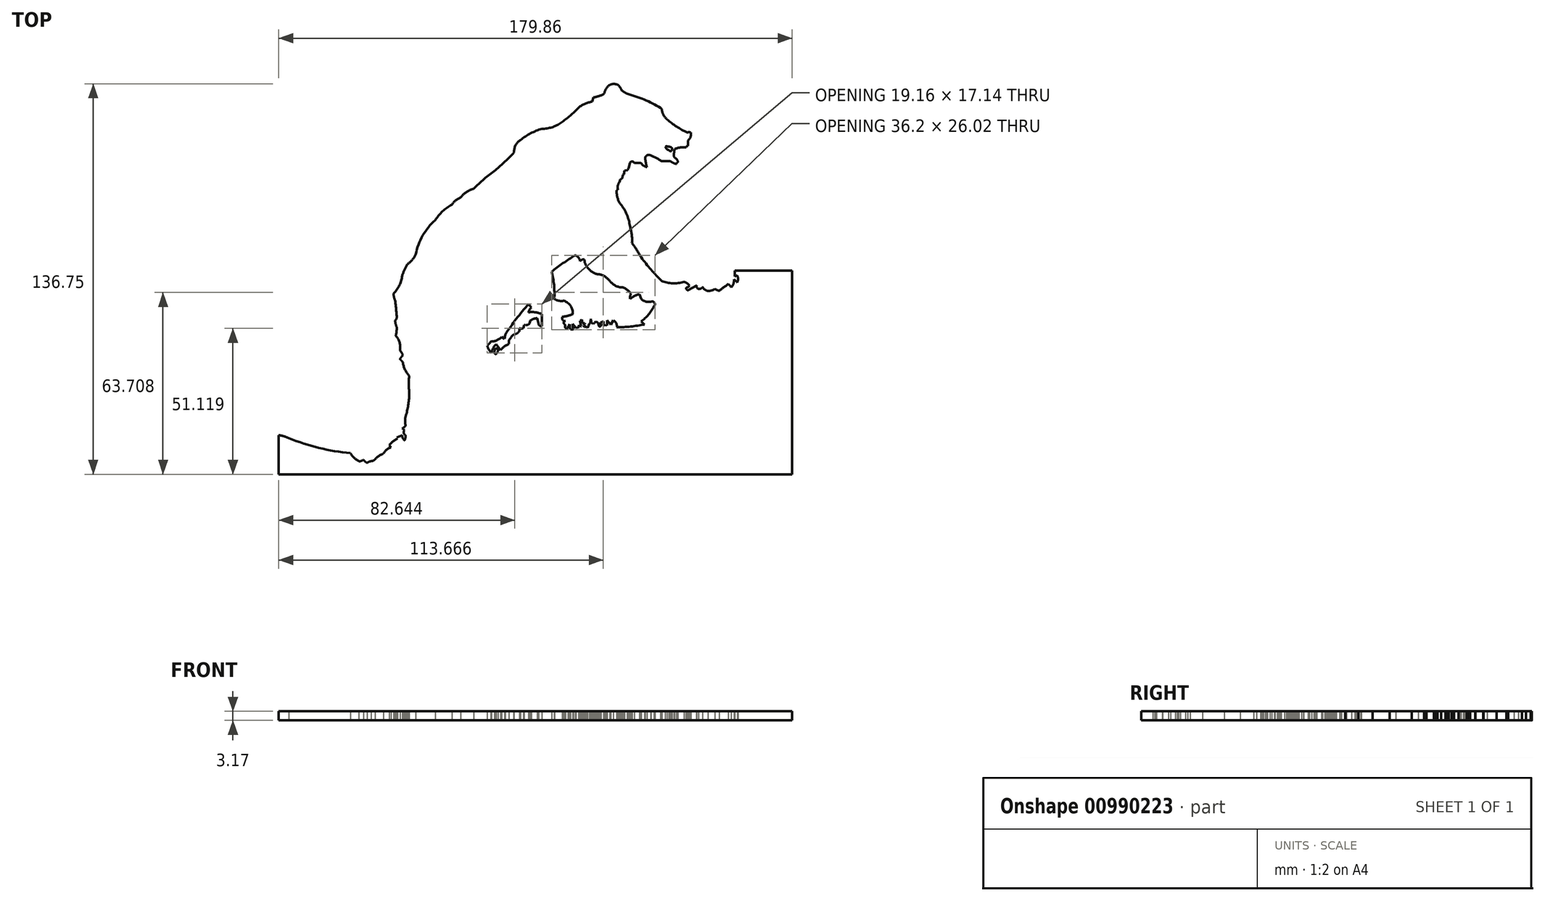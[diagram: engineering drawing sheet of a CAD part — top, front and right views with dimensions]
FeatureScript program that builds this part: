
annotation { "Feature Type Name" : "Feature", "Feature Type Description" : "" }
export const myFeature = defineFeature(function(context is Context, id is Id, definition is map)
    precondition{}
    {
        {
            var Q0;
            Q0=qCreatedBy(makeId("Top.planeOp"),FACE);
            var sketch = newSketch(context, id + "F0", { "sketchPlane" : qUnion([Q0])});
            skArc(sketch, "E0", {"start": v(84.74, 117.13) * mm, "mid": v(82.97, 115.24) * mm, "end": v(82.44, 112.7) * mm});
            skArc(sketch, "E1", {"start": v(75.9, 106.56) * mm, "mid": v(79.27, 109.53) * mm, "end": v(82.44, 112.7) * mm});
            skArc(sketch, "E2", {"start": v(75.9, 106.56) * mm, "mid": v(71.95, 103.44) * mm, "end": v(68.26, 100.02) * mm});
            skArc(sketch, "E3", {"start": v(68.26, 100.02) * mm, "mid": v(67.47, 99.77) * mm, "end": v(66.7, 99.44) * mm});
            skArc(sketch, "E4", {"start": v(66.7, 99.44) * mm, "mid": v(65.08, 98.39) * mm, "end": v(63.77, 96.95) * mm});
            skArc(sketch, "E5", {"start": v(63.77, 96.95) * mm, "mid": v(62.01, 95.94) * mm, "end": v(60.66, 94.42) * mm});
            skArc(sketch, "E6", {"start": v(60.66, 94.42) * mm, "mid": v(57.42, 92.12) * mm, "end": v(54.88, 89.06) * mm});
            skArc(sketch, "E7", {"start": v(54.88, 89.06) * mm, "mid": v(50.44, 83.63) * mm, "end": v(48, 77.05) * mm});
            skArc(sketch, "E8", {"start": v(45.04, 73.58) * mm, "mid": v(46.77, 75.1) * mm, "end": v(48, 77.05) * mm});
            skArc(sketch, "E9", {"start": v(45.04, 73.58) * mm, "mid": v(44.05, 71.63) * mm, "end": v(43.23, 69.6) * mm});
            skArc(sketch, "E10", {"start": v(40.26, 63.38) * mm, "mid": v(42.3, 66.22) * mm, "end": v(43.23, 69.6) * mm});
            skArc(sketch, "E11", {"start": v(40.26, 63.38) * mm, "mid": v(40.38, 62.12) * mm, "end": v(40.77, 60.92) * mm});
            skArc(sketch, "E12", {"start": v(41.35, 55.06) * mm, "mid": v(41.1, 58) * mm, "end": v(40.77, 60.92) * mm});
            skArc(sketch, "E13", {"start": v(40.77, 53.87) * mm, "mid": v(41.2, 54.4) * mm, "end": v(41.35, 55.06) * mm});
            skArc(sketch, "E14", {"start": v(40.77, 53.87) * mm, "mid": v(40.96, 52.69) * mm, "end": v(41.35, 51.55) * mm});
            skArc(sketch, "E15", {"start": v(41.02, 48.52) * mm, "mid": v(41.28, 50.03) * mm, "end": v(41.35, 51.55) * mm});
            skArc(sketch, "E16", {"start": v(42.47, 43.34) * mm, "mid": v(42.37, 46.1) * mm, "end": v(41.02, 48.52) * mm});
            skArc(sketch, "E17", {"start": v(43.48, 41.72) * mm, "mid": v(43.1, 42.6) * mm, "end": v(42.47, 43.34) * mm});
            skArc(sketch, "E18", {"start": v(43.48, 41.72) * mm, "mid": v(42.92, 41.07) * mm, "end": v(42.47, 40.34) * mm});
            skArc(sketch, "E19", {"start": v(43.48, 39.26) * mm, "mid": v(42.98, 39.8) * mm, "end": v(42.47, 40.34) * mm});
            skArc(sketch, "E20", {"start": v(43.48, 39.26) * mm, "mid": v(44.22, 36.72) * mm, "end": v(45.72, 34.55) * mm});
            skArc(sketch, "E21", {"start": v(45.72, 34.55) * mm, "mid": v(45.54, 31.76) * mm, "end": v(45.72, 28.96) * mm});
            skArc(sketch, "E22", {"start": v(44.76, 21.36) * mm, "mid": v(45.5, 25.13) * mm, "end": v(45.72, 28.96) * mm});
            skArc(sketch, "E23", {"start": v(44.76, 21.36) * mm, "mid": v(44.28, 19.27) * mm, "end": v(44.47, 17.14) * mm});
            skArc(sketch, "E24", {"start": v(43.23, 16.13) * mm, "mid": v(43.96, 16.5) * mm, "end": v(44.47, 17.14) * mm});
            skArc(sketch, "E25", {"start": v(44.04, 15.47) * mm, "mid": v(43.65, 15.82) * mm, "end": v(43.23, 16.13) * mm});
            skArc(sketch, "E26", {"start": v(44.04, 15.47) * mm, "mid": v(43.8, 14.48) * mm, "end": v(44.47, 13.7) * mm});
            skArc(sketch, "E27", {"start": v(44.04, 11.87) * mm, "mid": v(44.4, 12.75) * mm, "end": v(44.47, 13.7) * mm});
            skArc(sketch, "E28", {"start": v(43.23, 13.7) * mm, "mid": v(43.48, 12.71) * mm, "end": v(44.04, 11.87) * mm});
            skLineSegment(sketch, "E29", {"start": v(43.23, 13.7) * mm, "end": v(41.39, 12.99) * mm});
            skLineSegment(sketch, "E30", {"start": v(41.39, 12.99) * mm, "end": v(41.57, 12.5) * mm});
            skArc(sketch, "E31", {"start": v(41.57, 12.5) * mm, "mid": v(40.04, 11.56) * mm, "end": v(38.76, 10.28) * mm});
            skArc(sketch, "E32", {"start": v(39.36, 9.44) * mm, "mid": v(37.78, 8.63) * mm, "end": v(36.66, 7.25) * mm});
            skArc(sketch, "E33", {"start": v(36.66, 7.25) * mm, "mid": v(35.1, 6.45) * mm, "end": v(33.8, 5.3) * mm});
            skArc(sketch, "E34", {"start": v(32.36, 4.63) * mm, "mid": v(33.15, 4.8) * mm, "end": v(33.8, 5.3) * mm});
            skArc(sketch, "E35", {"start": v(32.36, 4.63) * mm, "mid": v(31.6, 4.4) * mm, "end": v(30.92, 4.02) * mm});
            skArc(sketch, "E36", {"start": v(29.64, 5.1) * mm, "mid": v(30.27, 4.55) * mm, "end": v(30.92, 4.02) * mm});
            skArc(sketch, "E37", {"start": v(28.03, 4.63) * mm, "mid": v(28.9, 4.68) * mm, "end": v(29.64, 5.1) * mm});
            skLineSegment(sketch, "E38", {"start": v(39.36, 9.44) * mm, "end": v(38.76, 10.28) * mm});
            skArc(sketch, "E39", {"start": v(25.08, 7.49) * mm, "mid": v(26.36, 5.86) * mm, "end": v(28.03, 4.63) * mm});
            skArc(sketch, "E40", {"start": v(3.55, 12.71) * mm, "mid": v(14.1, 9.26) * mm, "end": v(25.08, 7.49) * mm});
            skArc(sketch, "E41", {"start": v(3.55, 12.71) * mm, "mid": v(1.81, 13.35) * mm, "end": v(0, 13.7) * mm});
            skArc(sketch, "E42", {"start": v(92.2, 121.04) * mm, "mid": v(88.28, 119.45) * mm, "end": v(84.74, 117.13) * mm});
            skArc(sketch, "E43", {"start": v(92.2, 121.04) * mm, "mid": v(95.7, 121.57) * mm, "end": v(98.86, 123.14) * mm});
            skArc(sketch, "E44", {"start": v(98.86, 123.14) * mm, "mid": v(102.08, 125.64) * mm, "end": v(105.06, 128.42) * mm});
            skArc(sketch, "E45", {"start": v(109.8, 130.52) * mm, "mid": v(107.28, 129.82) * mm, "end": v(105.06, 128.42) * mm});
            skArc(sketch, "E46", {"start": v(110.16, 132.02) * mm, "mid": v(112.17, 132.46) * mm, "end": v(114.04, 133.3) * mm});
            skArc(sketch, "E47", {"start": v(115.9, 136.35) * mm, "mid": v(114.66, 135.01) * mm, "end": v(114.04, 133.3) * mm});
            skArc(sketch, "E48", {"start": v(118.82, 136.35) * mm, "mid": v(117.36, 136.75) * mm, "end": v(115.9, 136.35) * mm});
            skArc(sketch, "E49", {"start": v(120.05, 134.62) * mm, "mid": v(119.55, 135.57) * mm, "end": v(118.82, 136.35) * mm});
            skArc(sketch, "E50", {"start": v(120.05, 134.62) * mm, "mid": v(121, 133.9) * mm, "end": v(122.06, 133.3) * mm});
            skArc(sketch, "E51", {"start": v(133.72, 128.42) * mm, "mid": v(128.05, 131.24) * mm, "end": v(122.06, 133.3) * mm});
            skArc(sketch, "E52", {"start": v(134.23, 127.88) * mm, "mid": v(134.74, 125.93) * mm, "end": v(136, 124.37) * mm});
            skArc(sketch, "E53", {"start": v(136, 124.37) * mm, "mid": v(139.39, 121.78) * mm, "end": v(143.11, 119.72) * mm});
            skArc(sketch, "E54", {"start": v(144.32, 119.72) * mm, "mid": v(143.72, 119.84) * mm, "end": v(143.11, 119.72) * mm});
            skArc(sketch, "E55", {"start": v(143.37, 116.96) * mm, "mid": v(144.26, 118.2) * mm, "end": v(144.32, 119.72) * mm});
            skLineSegment(sketch, "E56", {"start": v(134.23, 127.88) * mm, "end": v(133.72, 128.42) * mm});
            skLineSegment(sketch, "E57", {"start": v(143.37, 116.96) * mm, "end": v(143.37, 115.1) * mm});
            skArc(sketch, "E58", {"start": v(143.37, 115.1) * mm, "mid": v(142.93, 114.88) * mm, "end": v(142.64, 114.48) * mm});
            skArc(sketch, "E59", {"start": v(142.64, 114.48) * mm, "mid": v(140.65, 114.49) * mm, "end": v(138.72, 113.95) * mm});
            skArc(sketch, "E60", {"start": v(138.72, 113.95) * mm, "mid": v(138.47, 112.51) * mm, "end": v(138.5, 111.05) * mm});
            skArc(sketch, "E61", {"start": v(137.65, 114.48) * mm, "mid": v(136.55, 114.8) * mm, "end": v(135.4, 114.84) * mm});
            skArc(sketch, "E62", {"start": v(135.4, 114.84) * mm, "mid": v(135.86, 113.98) * mm, "end": v(136.7, 113.52) * mm});
            skArc(sketch, "E63", {"start": v(136.7, 113.52) * mm, "mid": v(137.03, 113.25) * mm, "end": v(137.45, 113.2) * mm});
            skArc(sketch, "E64", {"start": v(137.45, 113.2) * mm, "mid": v(137.73, 113.81) * mm, "end": v(137.65, 114.48) * mm});
            skArc(sketch, "E65", {"start": v(139.86, 109.47) * mm, "mid": v(139.34, 110.4) * mm, "end": v(138.5, 111.05) * mm});
            skArc(sketch, "E66", {"start": v(139.86, 109.47) * mm, "mid": v(139.5, 109.11) * mm, "end": v(139.28, 108.66) * mm});
            skArc(sketch, "E67", {"start": v(137.1, 109.7) * mm, "mid": v(138.15, 109.1) * mm, "end": v(139.28, 108.66) * mm});
            skArc(sketch, "E68", {"start": v(134.12, 109.7) * mm, "mid": v(132.23, 110.8) * mm, "end": v(130.24, 111.74) * mm});
            skArc(sketch, "E69", {"start": v(130.24, 111.74) * mm, "mid": v(128.93, 111.71) * mm, "end": v(128.37, 110.53) * mm});
            skLineSegment(sketch, "E70", {"start": v(137.1, 109.7) * mm, "end": v(134.12, 109.7) * mm});
            skArc(sketch, "E71", {"start": v(128.37, 110.53) * mm, "mid": v(128.6, 109.05) * mm, "end": v(128.98, 107.6) * mm});
            skArc(sketch, "E72", {"start": v(126.9, 109.12) * mm, "mid": v(127.77, 108.13) * mm, "end": v(128.98, 107.6) * mm});
            skArc(sketch, "E73", {"start": v(124.53, 109.12) * mm, "mid": v(123.78, 109.6) * mm, "end": v(123.03, 109.12) * mm});
            skLineSegment(sketch, "E74", {"start": v(126.9, 109.12) * mm, "end": v(124.53, 109.12) * mm});
            skLineSegment(sketch, "E75", {"start": v(123.03, 109.12) * mm, "end": v(122.57, 107.17) * mm});
            skLineSegment(sketch, "E76", {"start": v(122.57, 107.17) * mm, "end": v(122.3, 106.86) * mm});
            skLineSegment(sketch, "E77", {"start": v(122.3, 106.86) * mm, "end": v(122.3, 106.6) * mm});
            skLineSegment(sketch, "E78", {"start": v(122.3, 106.6) * mm, "end": v(121.12, 106.45) * mm});
            skLineSegment(sketch, "E79", {"start": v(121.12, 106.45) * mm, "end": v(120.9, 105.02) * mm});
            skLineSegment(sketch, "E80", {"start": v(120.9, 105.02) * mm, "end": v(120.54, 104.91) * mm});
            skLineSegment(sketch, "E81", {"start": v(120.54, 104.91) * mm, "end": v(120.42, 103.68) * mm});
            skLineSegment(sketch, "E82", {"start": v(120.42, 103.68) * mm, "end": v(120, 103.51) * mm});
            skLineSegment(sketch, "E83", {"start": v(120, 103.51) * mm, "end": v(119.57, 103.22) * mm});
            skLineSegment(sketch, "E84", {"start": v(119.57, 103.22) * mm, "end": v(119.36, 102.38) * mm});
            skArc(sketch, "E85", {"start": v(119.36, 102.38) * mm, "mid": v(118.79, 101.13) * mm, "end": v(118.84, 99.76) * mm});
            skArc(sketch, "E86", {"start": v(118.84, 99.76) * mm, "mid": v(118.45, 99.5) * mm, "end": v(118.38, 99.04) * mm});
            skArc(sketch, "E87", {"start": v(118.38, 99.04) * mm, "mid": v(118.71, 96.72) * mm, "end": v(119.73, 94.62) * mm});
            skArc(sketch, "E88", {"start": v(123, 86.95) * mm, "mid": v(121.92, 91.02) * mm, "end": v(119.73, 94.62) * mm});
            skArc(sketch, "E89", {"start": v(123.74, 81) * mm, "mid": v(123.66, 84.01) * mm, "end": v(123, 86.95) * mm});
            skArc(sketch, "E90", {"start": v(126.93, 76.01) * mm, "mid": v(125.44, 78.58) * mm, "end": v(123.74, 81) * mm});
            skArc(sketch, "E91", {"start": v(126.93, 76.01) * mm, "mid": v(130.4, 71.72) * mm, "end": v(134.16, 67.69) * mm});
            skArc(sketch, "E92", {"start": v(134.16, 67.69) * mm, "mid": v(138.01, 66.92) * mm, "end": v(141.91, 67.43) * mm});
            skArc(sketch, "E93", {"start": v(143.83, 66.14) * mm, "mid": v(142.98, 66.95) * mm, "end": v(141.91, 67.43) * mm});
            skArc(sketch, "E94", {"start": v(142.8, 65.45) * mm, "mid": v(143.43, 65.62) * mm, "end": v(143.83, 66.14) * mm});
            skArc(sketch, "E95", {"start": v(142.8, 65.45) * mm, "mid": v(142.83, 64.8) * mm, "end": v(143.38, 64.47) * mm});
            skArc(sketch, "E96", {"start": v(103.02, 56.1) * mm, "mid": v(102.27, 58.99) * mm, "end": v(99.9, 60.8) * mm});
            skArc(sketch, "E97", {"start": v(96.5, 61.46) * mm, "mid": v(96.44, 66.27) * mm, "end": v(95.57, 71) * mm});
            skArc(sketch, "E98", {"start": v(103.81, 76.72) * mm, "mid": v(99.61, 73.97) * mm, "end": v(95.57, 71) * mm});
            skArc(sketch, "E99", {"start": v(99.26, 55.16) * mm, "mid": v(101.17, 55.51) * mm, "end": v(103.02, 56.1) * mm});
            skArc(sketch, "E100", {"start": v(131.48, 58.89) * mm, "mid": v(131.6, 60.14) * mm, "end": v(130.4, 60.48) * mm});
            skArc(sketch, "E101", {"start": v(126.93, 61.46) * mm, "mid": v(128.53, 60.5) * mm, "end": v(130.4, 60.48) * mm});
            skArc(sketch, "E102", {"start": v(126.38, 63.08) * mm, "mid": v(124.59, 62.48) * mm, "end": v(123, 61.46) * mm});
            skArc(sketch, "E103", {"start": v(123.41, 63.3) * mm, "mid": v(123.08, 62.4) * mm, "end": v(123, 61.46) * mm});
            skArc(sketch, "E104", {"start": v(123.41, 63.3) * mm, "mid": v(122.22, 64.53) * mm, "end": v(120.77, 65.45) * mm});
            skArc(sketch, "E105", {"start": v(116.18, 67.43) * mm, "mid": v(118.26, 65.94) * mm, "end": v(120.77, 65.45) * mm});
            skArc(sketch, "E106", {"start": v(116.18, 67.43) * mm, "mid": v(114.5, 69.1) * mm, "end": v(112.34, 70.06) * mm});
            skArc(sketch, "E107", {"start": v(108.76, 71.8) * mm, "mid": v(110.36, 70.54) * mm, "end": v(112.34, 70.06) * mm});
            skArc(sketch, "E108", {"start": v(107.06, 75.3) * mm, "mid": v(107.56, 73.38) * mm, "end": v(108.76, 71.8) * mm});
            skArc(sketch, "E109", {"start": v(107.06, 75.3) * mm, "mid": v(106.23, 75.18) * mm, "end": v(105.54, 74.7) * mm});
            skArc(sketch, "E110", {"start": v(105.54, 74.7) * mm, "mid": v(105, 75.98) * mm, "end": v(103.81, 76.72) * mm});
            skArc(sketch, "E111", {"start": v(126.93, 53.55) * mm, "mid": v(129.53, 55.93) * mm, "end": v(131.48, 58.89) * mm});
            skArc(sketch, "E112", {"start": v(118.38, 51.5) * mm, "mid": v(123.26, 51.78) * mm, "end": v(128.1, 52.5) * mm});
            skArc(sketch, "E113", {"start": v(118.38, 51.5) * mm, "mid": v(118.22, 52.9) * mm, "end": v(117.21, 53.9) * mm});
            skLineSegment(sketch, "E114", {"start": v(128.1, 52.5) * mm, "end": v(126.93, 53.55) * mm});
            skLineSegment(sketch, "E115", {"start": v(117.21, 53.9) * mm, "end": v(116.25, 52.5) * mm});
            skLineSegment(sketch, "E116", {"start": v(116.25, 52.5) * mm, "end": v(115.07, 53.9) * mm});
            skLineSegment(sketch, "E117", {"start": v(115.07, 53.9) * mm, "end": v(115.07, 52.13) * mm});
            skLineSegment(sketch, "E118", {"start": v(115.07, 52.13) * mm, "end": v(114.56, 52.32) * mm});
            skLineSegment(sketch, "E119", {"start": v(114.56, 52.32) * mm, "end": v(114.05, 52.13) * mm});
            skLineSegment(sketch, "E120", {"start": v(114.05, 52.13) * mm, "end": v(113.71, 52.32) * mm});
            skLineSegment(sketch, "E121", {"start": v(113.71, 52.32) * mm, "end": v(113.71, 53.55) * mm});
            skLineSegment(sketch, "E122", {"start": v(113.71, 53.55) * mm, "end": v(112.77, 53.25) * mm});
            skLineSegment(sketch, "E123", {"start": v(112.77, 53.25) * mm, "end": v(112.9, 52.13) * mm});
            skLineSegment(sketch, "E124", {"start": v(112.08, 52.1) * mm, "end": v(111.83, 53.01) * mm});
            skLineSegment(sketch, "E125", {"start": v(111.83, 53.01) * mm, "end": v(111.43, 53.37) * mm});
            skLineSegment(sketch, "E126", {"start": v(111.43, 53.37) * mm, "end": v(111.1, 53.46) * mm});
            skLineSegment(sketch, "E127", {"start": v(111.1, 53.46) * mm, "end": v(110.64, 53.21) * mm});
            skLineSegment(sketch, "E128", {"start": v(110.64, 53.21) * mm, "end": v(110.56, 52.8) * mm});
            skLineSegment(sketch, "E129", {"start": v(110.56, 52.8) * mm, "end": v(109.6, 52.96) * mm});
            skLineSegment(sketch, "E130", {"start": v(109.6, 52.96) * mm, "end": v(109.33, 54.42) * mm});
            skLineSegment(sketch, "E131", {"start": v(109.33, 54.42) * mm, "end": v(109.03, 52.78) * mm});
            skLineSegment(sketch, "E132", {"start": v(109.03, 52.78) * mm, "end": v(108.76, 52.83) * mm});
            skLineSegment(sketch, "E133", {"start": v(108.76, 52.83) * mm, "end": v(108.25, 51.24) * mm});
            skLineSegment(sketch, "E134", {"start": v(108.25, 51.24) * mm, "end": v(107.8, 51.78) * mm});
            skLineSegment(sketch, "E135", {"start": v(107.8, 51.78) * mm, "end": v(107.1, 51.53) * mm});
            skLineSegment(sketch, "E136", {"start": v(107.1, 51.53) * mm, "end": v(106.73, 52.2) * mm});
            skLineSegment(sketch, "E137", {"start": v(106.73, 52.2) * mm, "end": v(107.29, 52.54) * mm});
            skLineSegment(sketch, "E138", {"start": v(107.29, 52.54) * mm, "end": v(107.13, 52.92) * mm});
            skLineSegment(sketch, "E139", {"start": v(107.13, 52.92) * mm, "end": v(106.44, 52.92) * mm});
            skLineSegment(sketch, "E140", {"start": v(106.44, 52.92) * mm, "end": v(106.2, 54.19) * mm});
            skLineSegment(sketch, "E141", {"start": v(106.2, 54.19) * mm, "end": v(105.9, 53.84) * mm});
            skLineSegment(sketch, "E142", {"start": v(105.9, 53.84) * mm, "end": v(105.57, 53.84) * mm});
            skLineSegment(sketch, "E143", {"start": v(105.57, 53.84) * mm, "end": v(105.95, 51.93) * mm});
            skLineSegment(sketch, "E144", {"start": v(105.95, 51.93) * mm, "end": v(105.68, 51.67) * mm});
            skLineSegment(sketch, "E145", {"start": v(105.68, 51.67) * mm, "end": v(105.08, 52.32) * mm});
            skLineSegment(sketch, "E146", {"start": v(105.08, 52.32) * mm, "end": v(105.08, 51.51) * mm});
            skLineSegment(sketch, "E147", {"start": v(105.08, 51.51) * mm, "end": v(104.1, 51.3) * mm});
            skLineSegment(sketch, "E148", {"start": v(104.1, 51.3) * mm, "end": v(102.95, 52.69) * mm});
            skLineSegment(sketch, "E149", {"start": v(102.95, 52.69) * mm, "end": v(102.95, 51.53) * mm});
            skLineSegment(sketch, "E150", {"start": v(102.95, 51.53) * mm, "end": v(103.24, 50.91) * mm});
            skLineSegment(sketch, "E151", {"start": v(103.24, 50.91) * mm, "end": v(102.93, 50.7) * mm});
            skLineSegment(sketch, "E152", {"start": v(102.93, 50.7) * mm, "end": v(102.24, 50.8) * mm});
            skLineSegment(sketch, "E153", {"start": v(102.24, 50.8) * mm, "end": v(101.95, 51.3) * mm});
            skLineSegment(sketch, "E154", {"start": v(101.95, 51.3) * mm, "end": v(101.94, 52.54) * mm});
            skLineSegment(sketch, "E155", {"start": v(101.94, 52.54) * mm, "end": v(101.63, 51.9) * mm});
            skLineSegment(sketch, "E156", {"start": v(101.63, 51.9) * mm, "end": v(101.3, 51.87) * mm});
            skLineSegment(sketch, "E157", {"start": v(101.3, 51.87) * mm, "end": v(101.32, 51.5) * mm});
            skLineSegment(sketch, "E158", {"start": v(100.36, 51.53) * mm, "end": v(100.36, 52.38) * mm});
            skArc(sketch, "E159", {"start": v(99.26, 55.16) * mm, "mid": v(99.28, 54.53) * mm, "end": v(99.51, 53.93) * mm});
            skArc(sketch, "E160", {"start": v(99.51, 53.93) * mm, "mid": v(99.94, 53.74) * mm, "end": v(100.42, 53.74) * mm});
            skArc(sketch, "E161", {"start": v(100.42, 53.74) * mm, "mid": v(100.02, 53.46) * mm, "end": v(99.8, 53.03) * mm});
            skArc(sketch, "E162", {"start": v(99.8, 53.03) * mm, "mid": v(100.04, 52.67) * mm, "end": v(100.36, 52.38) * mm});
            skArc(sketch, "E163", {"start": v(100.36, 51.53) * mm, "mid": v(100.83, 51.05) * mm, "end": v(101.32, 51.5) * mm});
            skArc(sketch, "E164", {"start": v(112.08, 52.1) * mm, "mid": v(112.5, 51.8) * mm, "end": v(112.9, 52.13) * mm});
            skArc(sketch, "E165", {"start": v(96.5, 61.46) * mm, "mid": v(98.14, 60.8) * mm, "end": v(99.9, 60.8) * mm});
            skLineSegment(sketch, "E166", {"start": v(126.93, 61.46) * mm, "end": v(126.38, 63.08) * mm});
            skLineSegment(sketch, "E167", {"start": v(92.22, 51.95) * mm, "end": v(92.22, 56.07) * mm});
            skArc(sketch, "E168", {"start": v(92.22, 56.07) * mm, "mid": v(89.92, 56.77) * mm, "end": v(87.5, 56.77) * mm});
            skArc(sketch, "E169", {"start": v(88.47, 58.41) * mm, "mid": v(87.86, 57.67) * mm, "end": v(87.5, 56.77) * mm});
            skArc(sketch, "E170", {"start": v(87.5, 59.69) * mm, "mid": v(83.22, 54.45) * mm, "end": v(79.3, 48.93) * mm});
            skArc(sketch, "E171", {"start": v(74.34, 46.52) * mm, "mid": v(76.38, 46.95) * mm, "end": v(78.12, 48.11) * mm});
            skArc(sketch, "E172", {"start": v(90.56, 54.67) * mm, "mid": v(89.29, 54.46) * mm, "end": v(88.15, 53.85) * mm});
            skArc(sketch, "E173", {"start": v(85.96, 52.3) * mm, "mid": v(87.02, 52.32) * mm, "end": v(87.92, 52.9) * mm});
            skArc(sketch, "E174", {"start": v(84.32, 51.21) * mm, "mid": v(85, 51.03) * mm, "end": v(85.69, 51.21) * mm});
            skArc(sketch, "E175", {"start": v(82.27, 48.93) * mm, "mid": v(83.38, 49.35) * mm, "end": v(84.32, 50.07) * mm});
            skArc(sketch, "E176", {"start": v(82.27, 48.93) * mm, "mid": v(81.32, 47.92) * mm, "end": v(80.58, 46.74) * mm});
            skArc(sketch, "E177", {"start": v(80.63, 45.65) * mm, "mid": v(79.02, 44.76) * mm, "end": v(77.67, 43.5) * mm});
            skArc(sketch, "E178", {"start": v(77.67, 43.5) * mm, "mid": v(76.93, 44.57) * mm, "end": v(76.16, 45.6) * mm});
            skArc(sketch, "E179", {"start": v(76.16, 45.6) * mm, "mid": v(75.14, 44.19) * mm, "end": v(74.52, 42.55) * mm});
            skArc(sketch, "E180", {"start": v(73.06, 45.01) * mm, "mid": v(73.62, 43.68) * mm, "end": v(74.52, 42.55) * mm});
            skArc(sketch, "E181", {"start": v(73.06, 45.01) * mm, "mid": v(73.71, 45.75) * mm, "end": v(74.34, 46.52) * mm});
            skArc(sketch, "E182", {"start": v(91.02, 52.67) * mm, "mid": v(91.46, 52.04) * mm, "end": v(92.22, 51.95) * mm});
            skLineSegment(sketch, "E183", {"start": v(91.02, 52.67) * mm, "end": v(90.56, 54.67) * mm});
            skLineSegment(sketch, "E184", {"start": v(88.47, 58.41) * mm, "end": v(87.5, 59.69) * mm});
            skLineSegment(sketch, "E185", {"start": v(79.3, 48.93) * mm, "end": v(79.15, 47.53) * mm});
            skLineSegment(sketch, "E186", {"start": v(79.15, 47.53) * mm, "end": v(78.12, 48.11) * mm});
            skLineSegment(sketch, "E187", {"start": v(80.63, 45.65) * mm, "end": v(80.58, 46.74) * mm});
            skLineSegment(sketch, "E188", {"start": v(84.32, 50.07) * mm, "end": v(84.32, 51.21) * mm});
            skLineSegment(sketch, "E189", {"start": v(85.69, 51.21) * mm, "end": v(85.96, 52.3) * mm});
            skLineSegment(sketch, "E190", {"start": v(88.15, 53.85) * mm, "end": v(87.92, 52.9) * mm});
            skArc(sketch, "E191", {"start": v(76.87, 43.48) * mm, "mid": v(76.33, 44.08) * mm, "end": v(75.62, 43.7) * mm});
            skArc(sketch, "E192", {"start": v(76.22, 42.25) * mm, "mid": v(76.62, 42.82) * mm, "end": v(76.87, 43.48) * mm});
            skArc(sketch, "E193", {"start": v(75.53, 42.7) * mm, "mid": v(75.73, 42.25) * mm, "end": v(76.22, 42.25) * mm});
            skLineSegment(sketch, "E194", {"start": v(75.53, 42.7) * mm, "end": v(75.62, 43.7) * mm});
            skLineSegment(sketch, "E195", {"start": v(143.38, 64.47) * mm, "end": v(146.37, 66.14) * mm});
            skArc(sketch, "E196", {"start": v(146.37, 66.14) * mm, "mid": v(146.44, 65.41) * mm, "end": v(147, 64.96) * mm});
            skArc(sketch, "E197", {"start": v(147, 64.96) * mm, "mid": v(147.84, 65.06) * mm, "end": v(148.44, 65.65) * mm});
            skArc(sketch, "E198", {"start": v(148.44, 65.65) * mm, "mid": v(149.21, 64.73) * mm, "end": v(150.3, 64.24) * mm});
            skArc(sketch, "E199", {"start": v(152.78, 64.96) * mm, "mid": v(153.51, 64.56) * mm, "end": v(154.3, 64.27) * mm});
            skArc(sketch, "E200", {"start": v(157.49, 66.6) * mm, "mid": v(155.83, 65.51) * mm, "end": v(154.3, 64.27) * mm});
            skArc(sketch, "E201", {"start": v(158.5, 65.48) * mm, "mid": v(158.04, 66.08) * mm, "end": v(157.49, 66.6) * mm});
            skArc(sketch, "E202", {"start": v(158.5, 65.48) * mm, "mid": v(159.26, 66.77) * mm, "end": v(159.52, 68.26) * mm});
            skArc(sketch, "E203", {"start": v(160.61, 67.23) * mm, "mid": v(160.1, 67.77) * mm, "end": v(159.52, 68.26) * mm});
            skArc(sketch, "E204", {"start": v(150.3, 64.24) * mm, "mid": v(151.6, 64.4) * mm, "end": v(152.78, 64.96) * mm});
            skArc(sketch, "E205", {"start": v(160.61, 67.23) * mm, "mid": v(160.9, 68.44) * mm, "end": v(160.61, 69.65) * mm});
            skLineSegment(sketch, "E206", {"start": v(160.61, 69.65) * mm, "end": v(159.72, 69.38) * mm});
            skLineSegment(sketch, "E207", {"start": v(159.72, 69.38) * mm, "end": v(159.72, 70.72) * mm});
            skLineSegment(sketch, "E208", {"start": v(159.72, 70.72) * mm, "end": v(159.72, 71.4) * mm});
            skLineSegment(sketch, "E209", {"start": v(159.72, 71.4) * mm, "end": v(179.86, 71.4) * mm});
            skLineSegment(sketch, "E210", {"start": v(179.86, 71.4) * mm, "end": v(179.86, 0) * mm});
            skLineSegment(sketch, "E211", {"start": v(179.86, 0) * mm, "end": v(0, 0) * mm});
            skLineSegment(sketch, "E212", {"start": v(0, 13.7) * mm, "end": v(0, 0) * mm});
            skLineSegment(sketch, "E213", {"start": v(109.8, 130.52) * mm, "end": v(110.16, 132.02) * mm});
            skSolve(sketch);
        }
        {
            var Q0;
            Q0=makeQuery(id+"F0.imprint","IMPRINT",FACE,{"disambiguationData":[TD([[makeQuery(id+"F0.imprint","IMPRINT",EDGE,{"derivedFrom":sQuery(id+"F0.wireOp",EDGE,"E0")}),1.0]])]});
            extrude(context, id + "F1", {"entities" : qUnion([Q0]), "depth" : 3.17 * mm, "offsetDistance" : 25.4 * mm});
        }
    });
